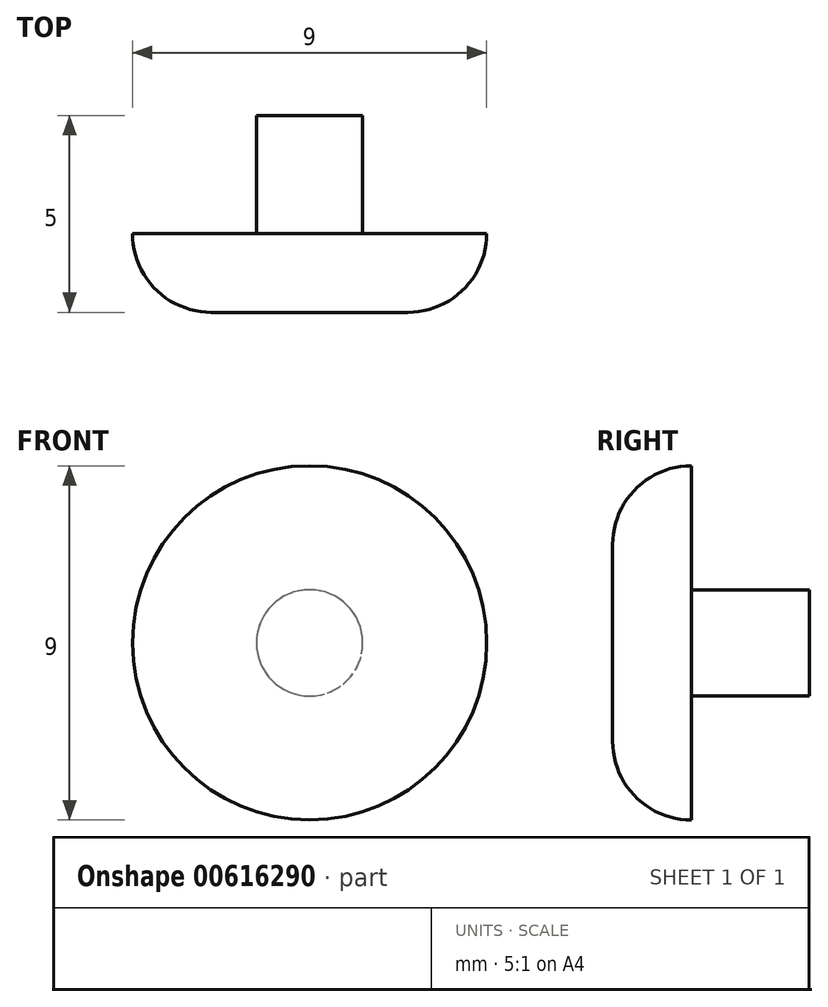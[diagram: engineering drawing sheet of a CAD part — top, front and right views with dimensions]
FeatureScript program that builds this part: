
annotation { "Feature Type Name" : "Feature", "Feature Type Description" : "" }
export const myFeature = defineFeature(function(context is Context, id is Id, definition is map)
    precondition{}
    {
        {
            var Q0;
            Q0=qCreatedBy(makeId("Front.planeOp"),FACE);
            var sketch = newSketch(context, id + "F0", { "sketchPlane" : qUnion([Q0])});
            skCircle(sketch, "E0", {"center": v(0, 0) * mm, "radius": 4.5 * mm});
            skSolve(sketch);
        }
        {
            var Q0;
            Q0=makeQuery(id+"F0.imprint","IMPRINT",FACE,{"disambiguationData":[TD([[makeQuery(id+"F0.imprint","IMPRINT",EDGE,{"derivedFrom":sQuery(id+"F0.wireOp",EDGE,"E0")}),1.0]])]});
            extrude(context, id + "F1", {"entities" : qUnion([Q0]), "depth" : 2 * mm, "offsetDistance" : 25 * mm});
        }
        {
            var Q0;
            Q0=makeQuery(id+"F1.opExtrude","CAP_EDGE",EDGE,{"disambiguationData":[OSD([sQuery(id+"F0.wireOp",EDGE,"E0")])],"isStart":false});
            fillet(context, id + "F2", {"entities" : qUnion([Q0]), "radius" : 2 * mm, "tangentPropagation" : true, "allowEdgeOverflow" : false});
        }
        {
            var Q0;
            Q0=makeQuery(id+"F1.opExtrude","CAP_FACE",FACE,{"disambiguationData":[OSD([sQuery(id+"F0.wireOp",EDGE,"E0")])],"isStart":true});
            var sketch = newSketch(context, id + "F3", { "sketchPlane" : qUnion([Q0])});
            skCircle(sketch, "E1", {"center": v(0, 0) * mm, "radius": 1.35 * mm});
            skSolve(sketch);
        }
        {
            var Q0;
            Q0=makeQuery(id+"F3.imprint","IMPRINT",FACE,{"disambiguationData":[TD([[makeQuery(id+"F3.imprint","IMPRINT",EDGE,{"derivedFrom":sQuery(id+"F3.wireOp",EDGE,"E1")}),1.0]])]});
            extrude(context, id + "F4", {"entities" : qUnion([Q0]), "operationType" : NewBodyOperationType.ADD, "depth" : 3 * mm, "offsetDistance" : 25 * mm});
        }
    });
